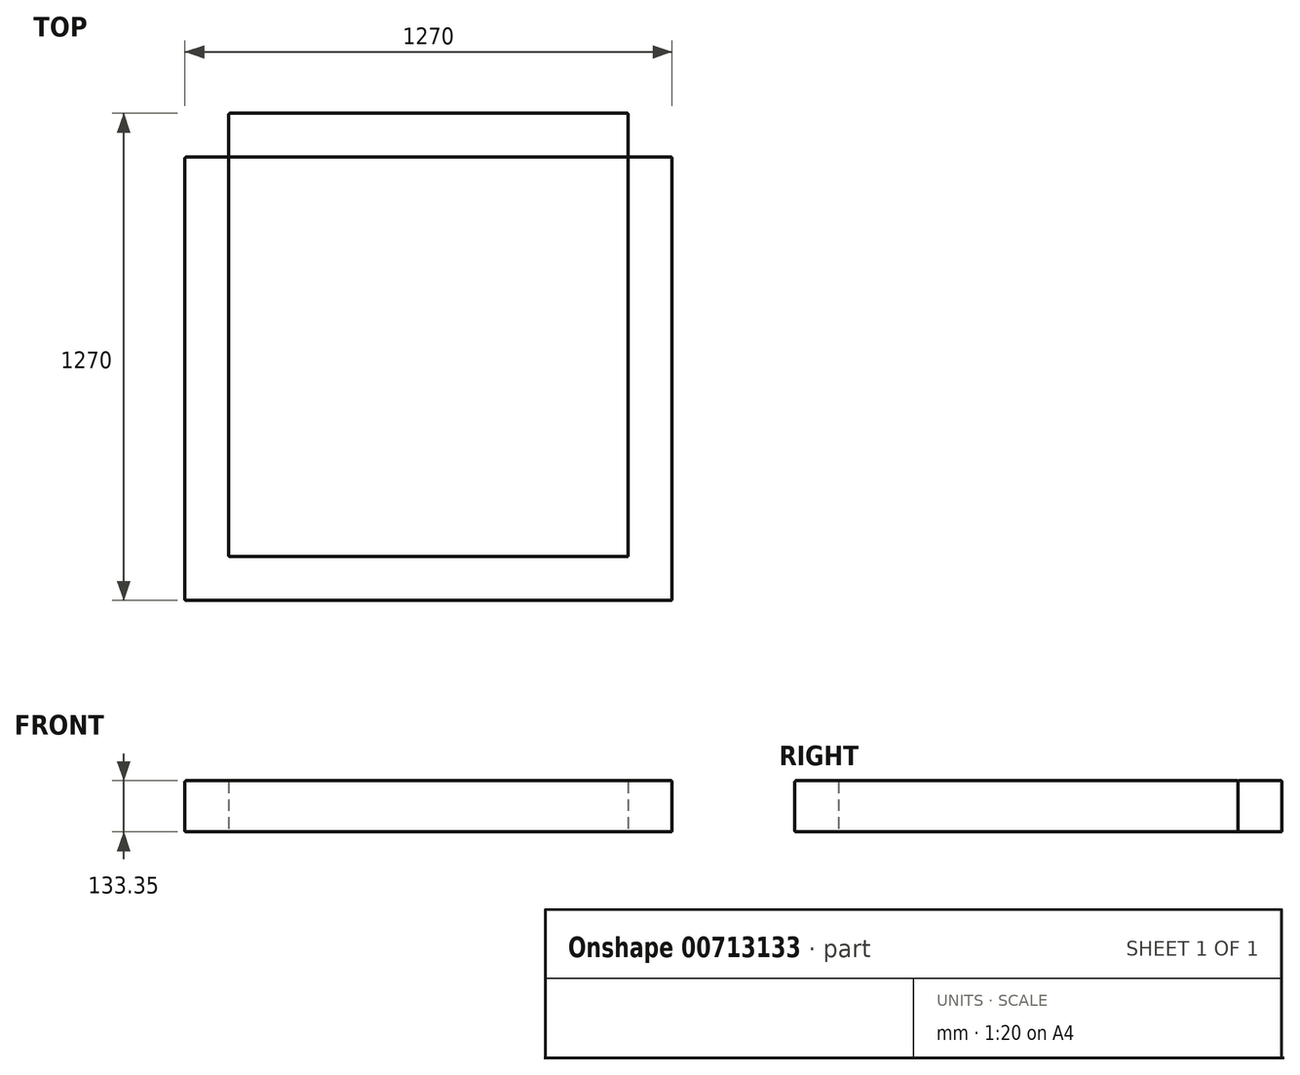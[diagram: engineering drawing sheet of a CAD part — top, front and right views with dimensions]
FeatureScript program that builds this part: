
annotation { "Feature Type Name" : "Feature", "Feature Type Description" : "" }
export const myFeature = defineFeature(function(context is Context, id is Id, definition is map)
    precondition{}
    {
        {
            var Q0;
            Q0=qCreatedBy(makeId("Top.planeOp"),FACE);
            var sketch = newSketch(context, id + "F0", { "sketchPlane" : qUnion([Q0])});
            skLineSegment(sketch, "E0", {"start": v(0, 0) * mm, "end": v(1270, 0) * mm});
            skLineSegment(sketch, "E1", {"start": v(1270, 0) * mm, "end": v(1270, 1155.7) * mm});
            skLineSegment(sketch, "E2", {"start": v(1270, 1155.7) * mm, "end": v(1155.7, 1155.7) * mm});
            skLineSegment(sketch, "E3", {"start": v(1155.7, 1155.7) * mm, "end": v(1155.7, 114.3) * mm});
            skLineSegment(sketch, "E4", {"start": v(1155.7, 114.3) * mm, "end": v(114.3, 114.3) * mm});
            skLineSegment(sketch, "E5", {"start": v(114.3, 114.3) * mm, "end": v(114.3, 1155.7) * mm});
            skLineSegment(sketch, "E6", {"start": v(114.3, 1155.7) * mm, "end": v(0, 1155.7) * mm});
            skLineSegment(sketch, "E7", {"start": v(0, 1155.7) * mm, "end": v(0, 0) * mm});
            skLineSegment(sketch, "E8", {"start": v(114.3, 1155.7) * mm, "end": v(1155.7, 1155.7) * mm});
            skLineSegment(sketch, "E9", {"start": v(114.3, 1155.7) * mm, "end": v(114.3, 1270) * mm});
            skLineSegment(sketch, "E10", {"start": v(114.3, 1270) * mm, "end": v(1155.7, 1270) * mm});
            skLineSegment(sketch, "E11", {"start": v(1155.7, 1270) * mm, "end": v(1155.7, 1155.7) * mm});
            skSolve(sketch);
        }
        {
            var Q0;
            Q0 = qSketchRegion(id + "F0", true);
            extrude(context, id + "F1", {"entities" : qUnion([Q0]), "depth" : 133.35 * mm, "offsetDistance" : 25.4 * mm});
        }
        {
            var Q0;
            Q0=makeQuery(id+"F0.imprint","IMPRINT",FACE,{"disambiguationData":[TD([[makeQuery(id+"F0.imprint","IMPRINT",EDGE,{"derivedFrom":sQuery(id+"F0.wireOp",EDGE,"E3")}),-1.0]])]});
            extrude(context, id + "F2", {"entities" : qUnion([Q0]), "operationType" : NewBodyOperationType.REMOVE, "endBound" : BoundingType.THROUGH_ALL, "depth" : 25.4 * mm, "offsetDistance" : 25.4 * mm});
        }
        {
            var Q0;
            Q0=makeQuery(id+"F1.opExtrude","SWEPT_EDGE",EDGE,{"disambiguationData":[OSD([sQuery(id+"F0.wireOp",EDGE,"E6"),sQuery(id+"F0.wireOp",EDGE,"E7")])]});
            var Q1;
            Q1=makeQuery(id+"F1.opExtrude","SWEPT_FACE",FACE,{"disambiguationData":[OSD([sQuery(id+"F0.wireOp",EDGE,"E6")])]});
            var Q2;
            Q2=makeQuery(id+"F1.opExtrude","SWEPT_FACE",FACE,{"disambiguationData":[OSD([sQuery(id+"F0.wireOp",EDGE,"E7")])]});
            var Q3;
            Q3=makeQuery(id+"F1.opExtrude","CAP_EDGE",EDGE,{"disambiguationData":[OSD([sQuery(id+"F0.wireOp",EDGE,"E0")])],"isStart":true});
            var Q4;
            Q4=makeQuery(id+"F1.opExtrude","CAP_EDGE",EDGE,{"disambiguationData":[OSD([sQuery(id+"F0.wireOp",EDGE,"E0")])],"isStart":false});
            var Q5;
            Q5=makeQuery(id+"F1.opExtrude","CAP_EDGE",EDGE,{"disambiguationData":[OSD([sQuery(id+"F0.wireOp",EDGE,"E2")])],"isStart":true});
            var Q6;
            Q6=makeQuery(id+"F1.opExtrude","CAP_EDGE",EDGE,{"disambiguationData":[OSD([sQuery(id+"F0.wireOp",EDGE,"E7")])],"isStart":false});
            var Q7;
            Q7=makeQuery(id+"F1.opExtrude","CAP_EDGE",EDGE,{"disambiguationData":[OSD([sQuery(id+"F0.wireOp",EDGE,"E7")])],"isStart":true});
            var Q8;
            Q8=makeQuery(id+"F2.boolean.opBoolean","COPY",EDGE,{"derivedFrom":makeQuery(id+"F2.opExtrude","SWEPT_EDGE",EDGE,{"disambiguationData":[OSD([sQuery(id+"F0.wireOp",EDGE,"E3"),sQuery(id+"F0.wireOp",EDGE,"E4")])]})});
            var Q9;
            Q9=makeQuery(id+"F2.boolean.opBoolean","COPY",EDGE,{"derivedFrom":makeQuery(id+"F2.opExtrude","SWEPT_EDGE",EDGE,{"disambiguationData":[OSD([sQuery(id+"F0.wireOp",EDGE,"E4"),sQuery(id+"F0.wireOp",EDGE,"E5")])]})});
            var Q10;
            Q10=makeQuery(id+"F1.opExtrude","CAP_EDGE",EDGE,{"disambiguationData":[OSD([sQuery(id+"F0.wireOp",EDGE,"E1")])],"isStart":true});
            var Q11;
            Q11=makeQuery(id+"F2.boolean.opBoolean","INTERSECT",EDGE,{"derivedFrom":[makeQuery(id+"F1.opExtrude","CAP_FACE",FACE,{"disambiguationData":[OSD([sQuery(id+"F0.wireOp",EDGE,"E0"),sQuery(id+"F0.wireOp",EDGE,"E1"),sQuery(id+"F0.wireOp",EDGE,"E2"),sQuery(id+"F0.wireOp",EDGE,"E6"),sQuery(id+"F0.wireOp",EDGE,"E7"),sQuery(id+"F0.wireOp",EDGE,"E9"),sQuery(id+"F0.wireOp",EDGE,"E10"),sQuery(id+"F0.wireOp",EDGE,"E11")])],"isStart":false}),makeQuery(id+"F2.opExtrude","SWEPT_FACE",FACE,{"disambiguationData":[OSD([sQuery(id+"F0.wireOp",EDGE,"E4")])]})]});
            var Q12;
            Q12=makeQuery(id+"F2.boolean.opBoolean","COPY",EDGE,{"derivedFrom":makeQuery(id+"F2.opExtrude","CAP_EDGE",EDGE,{"disambiguationData":[OSD([sQuery(id+"F0.wireOp",EDGE,"E3")])],"isStart":true})});
            var Q13;
            Q13=makeQuery(id+"F2.boolean.opBoolean","COPY",FACE,{"derivedFrom":makeQuery(id+"F2.opExtrude","SWEPT_FACE",FACE,{"disambiguationData":[OSD([sQuery(id+"F0.wireOp",EDGE,"E4")])]})});
            var Q14;
            {var subQ0=sQuery(id+"F0.wireOp",EDGE,"E6");var subQ1=sQuery(id+"F0.wireOp",EDGE,"E5");var subQ2=sQuery(id+"F0.wireOp",EDGE,"E9");var subQ3=sQuery(id+"F0.wireOp",EDGE,"E8");Q14=makeQuery(id+"F2.boolean.opBoolean","MERGE",EDGE,{"disambiguationData":[topologyDisambiguationEdgeConnected([makeQuery(id+"F1.opExtrude","SWEPT_FACE",FACE,{"disambiguationData":[OSD([subQ0])]})])],"derivedFrom":[makeQuery(id+"F1.opExtrude","SWEPT_EDGE",EDGE,{"disambiguationData":[OSD([subQ1,subQ0,subQ3,subQ2])]}),makeQuery(id+"F2.opExtrude","SWEPT_EDGE",EDGE,{"disambiguationData":[OSD([subQ1,subQ0,subQ3,subQ2])]})]});}
            var Q15;
            Q15=makeQuery(id+"F2.boolean.opBoolean","INTERSECT",EDGE,{"derivedFrom":[makeQuery(id+"F1.opExtrude","CAP_FACE",FACE,{"disambiguationData":[OSD([sQuery(id+"F0.wireOp",EDGE,"E0"),sQuery(id+"F0.wireOp",EDGE,"E1"),sQuery(id+"F0.wireOp",EDGE,"E2"),sQuery(id+"F0.wireOp",EDGE,"E6"),sQuery(id+"F0.wireOp",EDGE,"E7"),sQuery(id+"F0.wireOp",EDGE,"E9"),sQuery(id+"F0.wireOp",EDGE,"E10"),sQuery(id+"F0.wireOp",EDGE,"E11")])],"isStart":false}),makeQuery(id+"F2.opExtrude","SWEPT_FACE",FACE,{"disambiguationData":[OSD([sQuery(id+"F0.wireOp",EDGE,"E5")])]})]});
            var Q16;
            {var subQ0=sQuery(id+"F0.wireOp",EDGE,"E2");var subQ1=sQuery(id+"F0.wireOp",EDGE,"E1");var subQ2=sQuery(id+"F0.wireOp",EDGE,"E6");var subQ3=sQuery(id+"F0.wireOp",EDGE,"E0");var subQ4=sQuery(id+"F0.wireOp",EDGE,"E7");Q16=makeQuery(id+"F2.boolean.opBoolean","SPLIT",FACE,{"disambiguationData":[TD([makeQuery(id+"F1.opExtrude","SWEPT_FACE",FACE,{"disambiguationData":[OSD([subQ3])]})])],"derivedFrom":makeQuery(id+"F1.opExtrude","CAP_FACE",FACE,{"disambiguationData":[OSD([subQ3,subQ1,subQ0,subQ2,subQ4,sQuery(id+"F0.wireOp",EDGE,"E9"),sQuery(id+"F0.wireOp",EDGE,"E10"),sQuery(id+"F0.wireOp",EDGE,"E11")])],"isStart":true})});}
            var Q17;
            Q17=makeQuery(id+"F2.boolean.opBoolean","COPY",EDGE,{"derivedFrom":makeQuery(id+"F2.opExtrude","CAP_EDGE",EDGE,{"disambiguationData":[OSD([sQuery(id+"F0.wireOp",EDGE,"E5")])],"isStart":true})});
            var Q18;
            Q18=makeQuery(id+"F2.boolean.opBoolean","COPY",FACE,{"derivedFrom":makeQuery(id+"F2.opExtrude","SWEPT_FACE",FACE,{"disambiguationData":[OSD([sQuery(id+"F0.wireOp",EDGE,"E5")])]})});
            var Q19;
            Q19=makeQuery(id+"F1.opExtrude","SWEPT_EDGE",EDGE,{"disambiguationData":[OSD([sQuery(id+"F0.wireOp",EDGE,"E0"),sQuery(id+"F0.wireOp",EDGE,"E1")])]});
            var Q20;
            Q20=makeQuery(id+"F1.opExtrude","SWEPT_FACE",FACE,{"disambiguationData":[OSD([sQuery(id+"F0.wireOp",EDGE,"E0")])]});
            var Q21;
            Q21=makeQuery(id+"F1.opExtrude","SWEPT_EDGE",EDGE,{"disambiguationData":[OSD([sQuery(id+"F0.wireOp",EDGE,"E0"),sQuery(id+"F0.wireOp",EDGE,"E7")])]});
            var Q22;
            Q22=makeQuery(id+"F1.opExtrude","SWEPT_EDGE",EDGE,{"disambiguationData":[OSD([sQuery(id+"F0.wireOp",EDGE,"E9"),sQuery(id+"F0.wireOp",EDGE,"E10")])]});
            var Q23;
            Q23=makeQuery(id+"F1.opExtrude","SWEPT_FACE",FACE,{"disambiguationData":[OSD([sQuery(id+"F0.wireOp",EDGE,"E9")])]});
            var Q24;
            {var subQ0=sQuery(id+"F0.wireOp",EDGE,"E9");var subQ1=sQuery(id+"F0.wireOp",EDGE,"E10");var subQ2=sQuery(id+"F0.wireOp",EDGE,"E11");Q24=makeQuery(id+"F2.boolean.opBoolean","SPLIT",FACE,{"disambiguationData":[TD([makeQuery(id+"F1.opExtrude","SWEPT_FACE",FACE,{"disambiguationData":[OSD([subQ0])]})])],"derivedFrom":makeQuery(id+"F1.opExtrude","CAP_FACE",FACE,{"disambiguationData":[OSD([sQuery(id+"F0.wireOp",EDGE,"E0"),sQuery(id+"F0.wireOp",EDGE,"E1"),sQuery(id+"F0.wireOp",EDGE,"E2"),sQuery(id+"F0.wireOp",EDGE,"E6"),sQuery(id+"F0.wireOp",EDGE,"E7"),subQ0,subQ1,subQ2])],"isStart":true})});}
            var Q25;
            Q25=makeQuery(id+"F1.opExtrude","CAP_EDGE",EDGE,{"disambiguationData":[OSD([sQuery(id+"F0.wireOp",EDGE,"E10")])],"isStart":true});
            var Q26;
            Q26=makeQuery(id+"F1.opExtrude","CAP_EDGE",EDGE,{"disambiguationData":[OSD([sQuery(id+"F0.wireOp",EDGE,"E11")])],"isStart":true});
            var Q27;
            Q27=makeQuery(id+"F2.boolean.opBoolean","COPY",EDGE,{"derivedFrom":makeQuery(id+"F2.opExtrude","CAP_EDGE",EDGE,{"disambiguationData":[OSD([sQuery(id+"F0.wireOp",EDGE,"E4")])],"isStart":true})});
            var Q28;
            Q28=makeQuery(id+"F1.opExtrude","CAP_EDGE",EDGE,{"disambiguationData":[OSD([sQuery(id+"F0.wireOp",EDGE,"E6")])],"isStart":false});
            var Q29;
            Q29=makeQuery(id+"F1.opExtrude","CAP_EDGE",EDGE,{"disambiguationData":[OSD([sQuery(id+"F0.wireOp",EDGE,"E6")])],"isStart":true});
            var Q30;
            Q30=makeQuery(id+"F1.opExtrude","CAP_EDGE",EDGE,{"disambiguationData":[OSD([sQuery(id+"F0.wireOp",EDGE,"E9")])],"isStart":true});
            var Q31;
            Q31=makeQuery(id+"F1.opExtrude","CAP_EDGE",EDGE,{"disambiguationData":[OSD([sQuery(id+"F0.wireOp",EDGE,"E9")])],"isStart":false});
            var Q32;
            Q32=makeQuery(id+"F2.boolean.opBoolean","COPY",EDGE,{"derivedFrom":makeQuery(id+"F2.opExtrude","CAP_EDGE",EDGE,{"disambiguationData":[OSD([sQuery(id+"F0.wireOp",EDGE,"E8")])],"isStart":true})});
            var Q33;
            {var subQ0=sQuery(id+"F0.wireOp",EDGE,"E9");var subQ1=sQuery(id+"F0.wireOp",EDGE,"E8");var subQ2=sQuery(id+"F0.wireOp",EDGE,"E6");var subQ3=sQuery(id+"F0.wireOp",EDGE,"E5");Q33=makeQuery(id+"F2.boolean.opBoolean","MERGE",EDGE,{"disambiguationData":[topologyDisambiguationEdgeConnected([makeQuery(id+"F1.opExtrude","SWEPT_FACE",FACE,{"disambiguationData":[OSD([subQ0])]})])],"derivedFrom":[makeQuery(id+"F1.opExtrude","SWEPT_EDGE",EDGE,{"disambiguationData":[OSD([subQ3,subQ2,subQ1,subQ0])]}),makeQuery(id+"F2.opExtrude","SWEPT_EDGE",EDGE,{"disambiguationData":[OSD([subQ3,subQ2,subQ1,subQ0])]})]});}
            var Q34;
            Q34=makeQuery(id+"F1.opExtrude","SWEPT_FACE",FACE,{"disambiguationData":[OSD([sQuery(id+"F0.wireOp",EDGE,"E2")])]});
            var Q35;
            Q35=makeQuery(id+"F1.opExtrude","SWEPT_FACE",FACE,{"disambiguationData":[OSD([sQuery(id+"F0.wireOp",EDGE,"E1")])]});
            var Q36;
            {var subQ0=sQuery(id+"F0.wireOp",EDGE,"E2");var subQ1=sQuery(id+"F0.wireOp",EDGE,"E3");var subQ2=sQuery(id+"F0.wireOp",EDGE,"E11");var subQ3=sQuery(id+"F0.wireOp",EDGE,"E8");Q36=makeQuery(id+"F2.boolean.opBoolean","MERGE",EDGE,{"disambiguationData":[topologyDisambiguationEdgeConnected([makeQuery(id+"F1.opExtrude","SWEPT_FACE",FACE,{"disambiguationData":[OSD([subQ0])]})])],"derivedFrom":[makeQuery(id+"F1.opExtrude","SWEPT_EDGE",EDGE,{"disambiguationData":[OSD([subQ0,subQ1,subQ3,subQ2])]}),makeQuery(id+"F2.opExtrude","SWEPT_EDGE",EDGE,{"disambiguationData":[OSD([subQ0,subQ1,subQ3,subQ2])]})]});}
            var Q37;
            Q37=makeQuery(id+"F1.opExtrude","CAP_EDGE",EDGE,{"disambiguationData":[OSD([sQuery(id+"F0.wireOp",EDGE,"E1")])],"isStart":false});
            var Q38;
            Q38=makeQuery(id+"F2.boolean.opBoolean","COPY",FACE,{"derivedFrom":makeQuery(id+"F2.opExtrude","SWEPT_FACE",FACE,{"disambiguationData":[OSD([sQuery(id+"F0.wireOp",EDGE,"E3")])]})});
            var Q39;
            {var subQ0=sQuery(id+"F0.wireOp",EDGE,"E2");var subQ1=sQuery(id+"F0.wireOp",EDGE,"E1");var subQ2=sQuery(id+"F0.wireOp",EDGE,"E6");var subQ3=sQuery(id+"F0.wireOp",EDGE,"E0");var subQ4=sQuery(id+"F0.wireOp",EDGE,"E7");Q39=makeQuery(id+"F2.boolean.opBoolean","SPLIT",FACE,{"disambiguationData":[TD([makeQuery(id+"F1.opExtrude","SWEPT_FACE",FACE,{"disambiguationData":[OSD([subQ3])]})])],"derivedFrom":makeQuery(id+"F1.opExtrude","CAP_FACE",FACE,{"disambiguationData":[OSD([subQ3,subQ1,subQ0,subQ2,subQ4,sQuery(id+"F0.wireOp",EDGE,"E9"),sQuery(id+"F0.wireOp",EDGE,"E10"),sQuery(id+"F0.wireOp",EDGE,"E11")])],"isStart":false})});}
            var Q40;
            Q40=makeQuery(id+"F2.boolean.opBoolean","INTERSECT",EDGE,{"derivedFrom":[makeQuery(id+"F1.opExtrude","CAP_FACE",FACE,{"disambiguationData":[OSD([sQuery(id+"F0.wireOp",EDGE,"E0"),sQuery(id+"F0.wireOp",EDGE,"E1"),sQuery(id+"F0.wireOp",EDGE,"E2"),sQuery(id+"F0.wireOp",EDGE,"E6"),sQuery(id+"F0.wireOp",EDGE,"E7"),sQuery(id+"F0.wireOp",EDGE,"E9"),sQuery(id+"F0.wireOp",EDGE,"E10"),sQuery(id+"F0.wireOp",EDGE,"E11")])],"isStart":false}),makeQuery(id+"F2.opExtrude","SWEPT_FACE",FACE,{"disambiguationData":[OSD([sQuery(id+"F0.wireOp",EDGE,"E3")])]})]});
            var Q41;
            Q41=makeQuery(id+"F1.opExtrude","SWEPT_FACE",FACE,{"disambiguationData":[OSD([sQuery(id+"F0.wireOp",EDGE,"E11")])]});
            var Q42;
            Q42=makeQuery(id+"F1.opExtrude","SWEPT_FACE",FACE,{"disambiguationData":[OSD([sQuery(id+"F0.wireOp",EDGE,"E10")])]});
            var Q43;
            Q43=makeQuery(id+"F2.boolean.opBoolean","INTERSECT",EDGE,{"derivedFrom":[makeQuery(id+"F1.opExtrude","CAP_FACE",FACE,{"disambiguationData":[OSD([sQuery(id+"F0.wireOp",EDGE,"E0"),sQuery(id+"F0.wireOp",EDGE,"E1"),sQuery(id+"F0.wireOp",EDGE,"E2"),sQuery(id+"F0.wireOp",EDGE,"E6"),sQuery(id+"F0.wireOp",EDGE,"E7"),sQuery(id+"F0.wireOp",EDGE,"E9"),sQuery(id+"F0.wireOp",EDGE,"E10"),sQuery(id+"F0.wireOp",EDGE,"E11")])],"isStart":false}),makeQuery(id+"F2.opExtrude","SWEPT_FACE",FACE,{"disambiguationData":[OSD([sQuery(id+"F0.wireOp",EDGE,"E8")])]})]});
            var Q44;
            {var subQ0=sQuery(id+"F0.wireOp",EDGE,"E9");var subQ1=sQuery(id+"F0.wireOp",EDGE,"E10");var subQ2=sQuery(id+"F0.wireOp",EDGE,"E11");Q44=makeQuery(id+"F2.boolean.opBoolean","SPLIT",FACE,{"disambiguationData":[TD([makeQuery(id+"F1.opExtrude","SWEPT_FACE",FACE,{"disambiguationData":[OSD([subQ0])]})])],"derivedFrom":makeQuery(id+"F1.opExtrude","CAP_FACE",FACE,{"disambiguationData":[OSD([sQuery(id+"F0.wireOp",EDGE,"E0"),sQuery(id+"F0.wireOp",EDGE,"E1"),sQuery(id+"F0.wireOp",EDGE,"E2"),sQuery(id+"F0.wireOp",EDGE,"E6"),sQuery(id+"F0.wireOp",EDGE,"E7"),subQ0,subQ1,subQ2])],"isStart":false})});}
            var Q45;
            Q45=makeQuery(id+"F1.opExtrude","CAP_EDGE",EDGE,{"disambiguationData":[OSD([sQuery(id+"F0.wireOp",EDGE,"E10")])],"isStart":false});
            var Q46;
            Q46=makeQuery(id+"F2.boolean.opBoolean","COPY",FACE,{"derivedFrom":makeQuery(id+"F2.opExtrude","SWEPT_FACE",FACE,{"disambiguationData":[OSD([sQuery(id+"F0.wireOp",EDGE,"E8")])]})});
            var Q47;
            Q47=makeQuery(id+"F1.opExtrude","SWEPT_EDGE",EDGE,{"disambiguationData":[OSD([sQuery(id+"F0.wireOp",EDGE,"E1"),sQuery(id+"F0.wireOp",EDGE,"E2")])]});
            var Q48;
            Q48=makeQuery(id+"F1.opExtrude","CAP_EDGE",EDGE,{"disambiguationData":[OSD([sQuery(id+"F0.wireOp",EDGE,"E2")])],"isStart":false});
            var Q49;
            Q49=makeQuery(id+"F1.opExtrude","SWEPT_EDGE",EDGE,{"disambiguationData":[OSD([sQuery(id+"F0.wireOp",EDGE,"E10"),sQuery(id+"F0.wireOp",EDGE,"E11")])]});
            var Q50;
            Q50=makeQuery(id+"F1.opExtrude","CAP_EDGE",EDGE,{"disambiguationData":[OSD([sQuery(id+"F0.wireOp",EDGE,"E11")])],"isStart":false});
            var Q51;
            {var subQ0=sQuery(id+"F0.wireOp",EDGE,"E11");var subQ1=sQuery(id+"F0.wireOp",EDGE,"E8");var subQ2=sQuery(id+"F0.wireOp",EDGE,"E3");var subQ3=sQuery(id+"F0.wireOp",EDGE,"E2");Q51=makeQuery(id+"F2.boolean.opBoolean","MERGE",EDGE,{"disambiguationData":[topologyDisambiguationEdgeConnected([makeQuery(id+"F1.opExtrude","SWEPT_FACE",FACE,{"disambiguationData":[OSD([subQ0])]})])],"derivedFrom":[makeQuery(id+"F1.opExtrude","SWEPT_EDGE",EDGE,{"disambiguationData":[OSD([subQ3,subQ2,subQ1,subQ0])]}),makeQuery(id+"F2.opExtrude","SWEPT_EDGE",EDGE,{"disambiguationData":[OSD([subQ3,subQ2,subQ1,subQ0])]})]});}
            fillet(context, id + "F3", {"entities" : qUnion([Q0, Q1, Q2, Q3, Q4, Q5, Q6, Q7, Q8, Q9, Q10, Q11, Q12, Q13, Q14, Q15, Q16, Q17, Q18, Q19, Q20, Q21, Q22, Q23, Q24, Q25, Q26, Q27, Q28, Q29, Q30, Q31, Q32, Q33, Q34, Q35, Q36, Q37, Q38, Q39, Q40, Q41, Q42, Q43, Q44, Q45, Q46, Q47, Q48, Q49, Q50, Q51]), "radius" : 2.54 * mm, "tangentPropagation" : true, "allowEdgeOverflow" : false});
        }
    });
